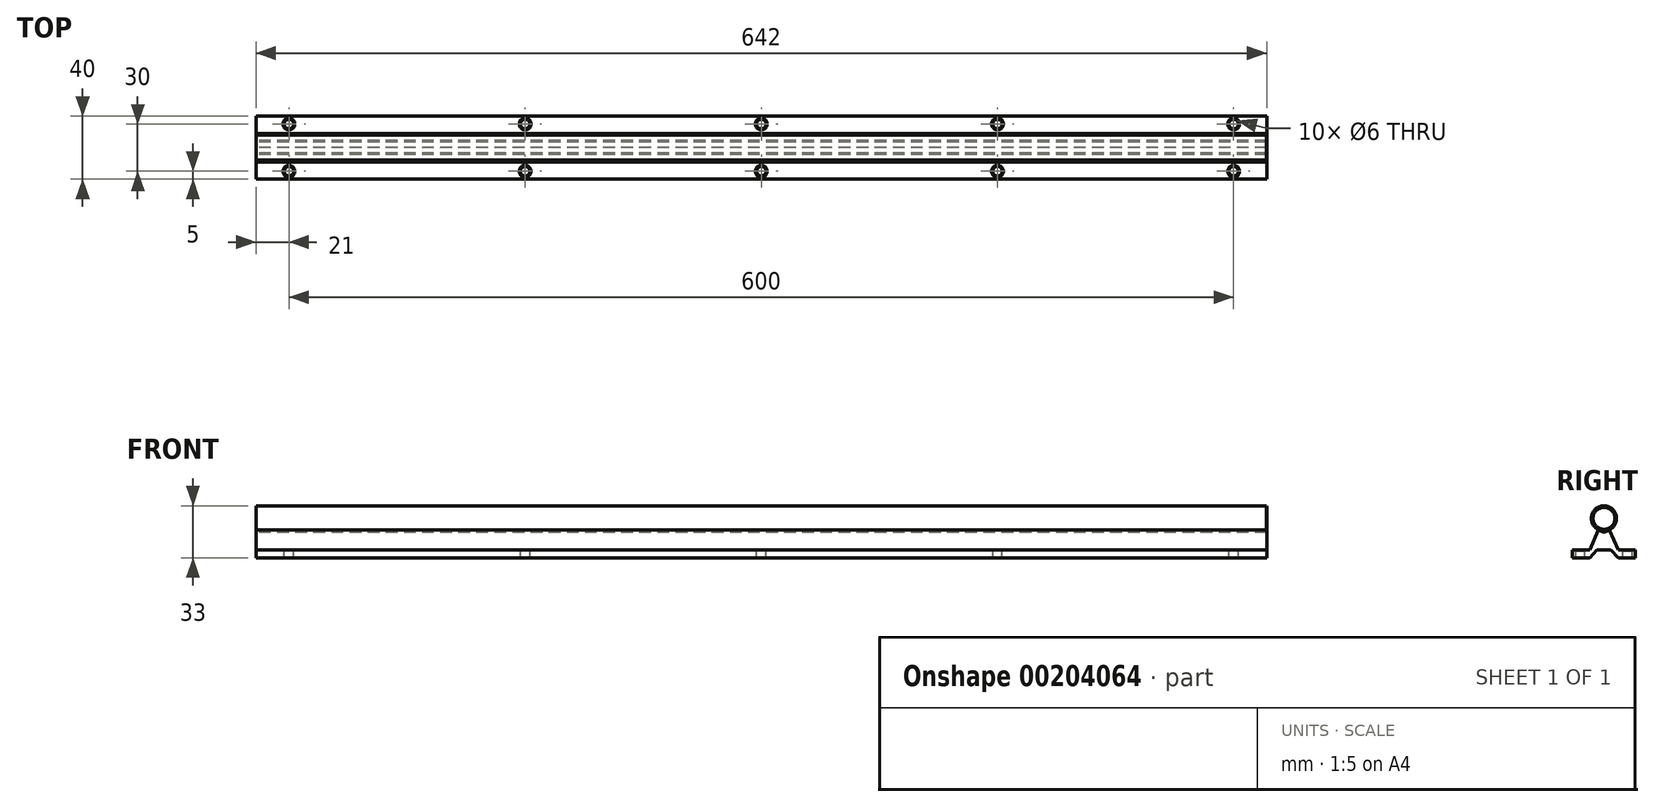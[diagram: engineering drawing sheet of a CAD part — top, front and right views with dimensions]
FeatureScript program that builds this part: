
annotation { "Feature Type Name" : "Feature", "Feature Type Description" : "" }
export const myFeature = defineFeature(function(context is Context, id is Id, definition is map)
    precondition{}
    {
        {
            var Q0;
            Q0=qCreatedBy(makeId("Right.planeOp"),FACE);
            var sketch = newSketch(context, id + "F0", { "sketchPlane" : qUnion([Q0])});
            skCircle(sketch, "E0", {"center": v(0, 25) * mm, "radius": 8 * mm});
            skLineSegment(sketch, "E1", {"start": v(0, 33) * mm, "end": v(0, 25) * mm, "construction": true});
            skLineSegment(sketch, "E2", {"start": v(0, 25) * mm, "end": v(0, 0) * mm, "construction": true});
            skLineSegment(sketch, "E3", {"start": v(0, 0) * mm, "end": v(9, 0) * mm, "construction": true});
            skLineSegment(sketch, "E4", {"start": v(9, 0) * mm, "end": v(20, 0) * mm});
            skLineSegment(sketch, "E5", {"start": v(20, 0) * mm, "end": v(20, 5) * mm});
            skLineSegment(sketch, "E6", {"start": v(20, 5) * mm, "end": v(9, 5) * mm});
            skLineSegment(sketch, "E7", {"start": v(9, 5) * mm, "end": v(3.5, 17.8) * mm});
            skLineSegment(sketch, "E8", {"start": v(3.5, 17.8) * mm, "end": v(0, 16.1) * mm});
            skLineSegment(sketch, "E9", {"start": v(0, 16.1) * mm, "end": v(0, 5) * mm});
            skLineSegment(sketch, "E10", {"start": v(0, 5) * mm, "end": v(4.5, 5) * mm});
            skLineSegment(sketch, "E11", {"start": v(4.5, 5) * mm, "end": v(9, 0) * mm});
            skLineSegment(sketch, "E12.MirrorCS", {"start": v(-20, 0) * mm, "end": v(-20, 5) * mm});
            skLineSegment(sketch, "E13.MirrorCS", {"start": v(-9, 0) * mm, "end": v(-20, 0) * mm});
            skLineSegment(sketch, "E14.MirrorCS", {"start": v(-4.5, 5) * mm, "end": v(-9, 0) * mm});
            skLineSegment(sketch, "E15.MirrorCS", {"start": v(-20, 5) * mm, "end": v(-9, 5) * mm});
            skLineSegment(sketch, "E16.MirrorCS", {"start": v(-9, 5) * mm, "end": v(-3.5, 17.8) * mm});
            skLineSegment(sketch, "E17.MirrorCS", {"start": v(-3.5, 17.8) * mm, "end": v(0, 16.1) * mm});
            skLineSegment(sketch, "E18.MirrorCS", {"start": v(0, 5) * mm, "end": v(-4.5, 5) * mm});
            skSolve(sketch);
        }
        {
            var Q0;
            Q0=makeQuery(id+"F0.imprint","IMPRINT",FACE,{"disambiguationData":[TD([[makeQuery(id+"F0.imprint","IMPRINT",EDGE,{"derivedFrom":sQuery(id+"F0.wireOp",EDGE,"E4")}),1.0]])]});
            var Q1;
            Q1=makeQuery(id+"F0.imprint","IMPRINT",FACE,{"disambiguationData":[TD([[makeQuery(id+"F0.imprint","IMPRINT",EDGE,{"derivedFrom":sQuery(id+"F0.wireOp",EDGE,"E9")}),-1.0]])]});
            extrude(context, id + "F1", {"entities" : qUnion([Q0, Q1]), "endBound" : BoundingType.SYMMETRIC, "depth" : 642 * mm});
        }
        {
            var Q0;
            {var subQ0=sQuery(id+"F0.wireOp",EDGE,"E0");var subQ1=makeQuery(id+"F0.imprint","INTERSECT",VERTEX,{"derivedFrom":[subQ0,sQuery(id+"F0.wireOp",EDGE,"E7"),sQuery(id+"F0.wireOp",EDGE,"E8")]});Q0=makeQuery(id+"F0.imprint","IMPRINT",FACE,{"disambiguationData":[TD([[makeQuery(id+"F0.imprint","IMPRINT",EDGE,{"disambiguationData":[TD([[subQ1,1.0]])],"derivedFrom":subQ0}),1.0]])]});}
            extrude(context, id + "F2", {"entities" : qUnion([Q0]), "endBound" : BoundingType.SYMMETRIC, "depth" : 642 * mm});
        }
        {
            var Q0;
            Q0=makeQuery(id+"F1.opExtrude","SWEPT_FACE",FACE,{"disambiguationData":[OSD([sQuery(id+"F0.wireOp",EDGE,"E15.MirrorCS")])]});
            var sketch = newSketch(context, id + "F3", { "sketchPlane" : qUnion([Q0])});
            skLineSegment(sketch, "E19", {"start": v(-321, 0) * mm, "end": v(321, 0) * mm, "construction": true});
            skLineSegment(sketch, "E20", {"start": v(-321, -15) * mm, "end": v(321, -15) * mm, "construction": true});
            skPoint(sketch, "E21", {"position": v(0, -15) * mm});
            skLineSegment(sketch, "E22", {"start": v(0, 0) * mm, "end": v(0, 49.58) * mm, "construction": true});
            skPoint(sketch, "E22.endSnap0", {"position": v(0, 0) * mm});
            skPoint(sketch, "E23", {"position": v(150, -15) * mm});
            skPoint(sketch, "E24", {"position": v(300, -15) * mm});
            skPoint(sketch, "E25.MirrorP", {"position": v(-300, -15) * mm});
            skPoint(sketch, "E26.MirrorP", {"position": v(-150, -15) * mm});
            skPoint(sketch, "E27.MirrorP", {"position": v(300, 15) * mm});
            skPoint(sketch, "E28.MirrorP", {"position": v(150, 15) * mm});
            skPoint(sketch, "E29.MirrorP", {"position": v(0, 15) * mm});
            skPoint(sketch, "E30.MirrorP", {"position": v(-150, 15) * mm});
            skPoint(sketch, "E31.MirrorP", {"position": v(-300, 15) * mm});
            skSolve(sketch);
        }
        {
            var Q0;
            Q0=sQuery(id+"F3.wireOp",VERTEX,"E30.MirrorP");
            var Q1;
            Q1=sQuery(id+"F3.wireOp",VERTEX,"E31.MirrorP");
            var Q2;
            Q2=sQuery(id+"F3.wireOp",VERTEX,"E29.MirrorP");
            var Q3;
            Q3=sQuery(id+"F3.wireOp",VERTEX,"E21");
            var Q4;
            Q4=sQuery(id+"F3.wireOp",VERTEX,"E25.MirrorP");
            var Q5;
            Q5=sQuery(id+"F3.wireOp",VERTEX,"E26.MirrorP");
            var Q6;
            Q6=sQuery(id+"F3.wireOp",VERTEX,"E23");
            var Q7;
            Q7=sQuery(id+"F3.wireOp",VERTEX,"E27.MirrorP");
            var Q8;
            Q8=sQuery(id+"F3.wireOp",VERTEX,"E28.MirrorP");
            var Q9;
            Q9=sQuery(id+"F3.wireOp",VERTEX,"E24");
            var Q10;
            Q10=makeQuery(id+"F1.opExtrude","SWEPT_BODY",BODY,{"disambiguationData":[OSD([sQuery(id+"F0.wireOp",EDGE,"E4"),sQuery(id+"F0.wireOp",EDGE,"E5"),sQuery(id+"F0.wireOp",EDGE,"E6"),sQuery(id+"F0.wireOp",EDGE,"E7"),sQuery(id+"F0.wireOp",EDGE,"E8"),sQuery(id+"F0.wireOp",EDGE,"E10"),sQuery(id+"F0.wireOp",EDGE,"E11"),sQuery(id+"F0.wireOp",EDGE,"E12.MirrorCS"),sQuery(id+"F0.wireOp",EDGE,"E13.MirrorCS"),sQuery(id+"F0.wireOp",EDGE,"E14.MirrorCS"),sQuery(id+"F0.wireOp",EDGE,"E15.MirrorCS"),sQuery(id+"F0.wireOp",EDGE,"E16.MirrorCS"),sQuery(id+"F0.wireOp",EDGE,"E17.MirrorCS"),sQuery(id+"F0.wireOp",EDGE,"E18.MirrorCS")])]});
            hole(context, id + "F4", {"style" : HoleStyle.C_SINK, "endStyle" : HoleEndStyle.THROUGH, "holeDiameter" : 6 * mm, "cSinkDiameter" : 7.5 * mm, "cSinkAngle" : 90 * degree, "locations" : qUnion([Q0, Q1, Q2, Q3, Q4, Q5, Q6, Q7, Q8, Q9]), "scope" : qUnion([Q10]), "isTappedThrough" : true});
        }
        {
            var Q0;
            Q0=makeQuery(id+"F2.opExtrude","CAP_EDGE",EDGE,{"disambiguationData":[OSD([sQuery(id+"F0.wireOp",EDGE,"E0")])],"isStart":false});
            var Q1;
            Q1=makeQuery(id+"F2.opExtrude","CAP_EDGE",EDGE,{"disambiguationData":[OSD([sQuery(id+"F0.wireOp",EDGE,"E0")])],"isStart":true});
            chamfer(context, id + "F5", {"entities" : qUnion([Q0, Q1]), "chamferType" : ChamferType.TWO_OFFSETS, "width1" : 1 * mm, "oppositeDirection" : false, "width2" : .2 * mm, "tangentPropagation" : true});
        }
    });
